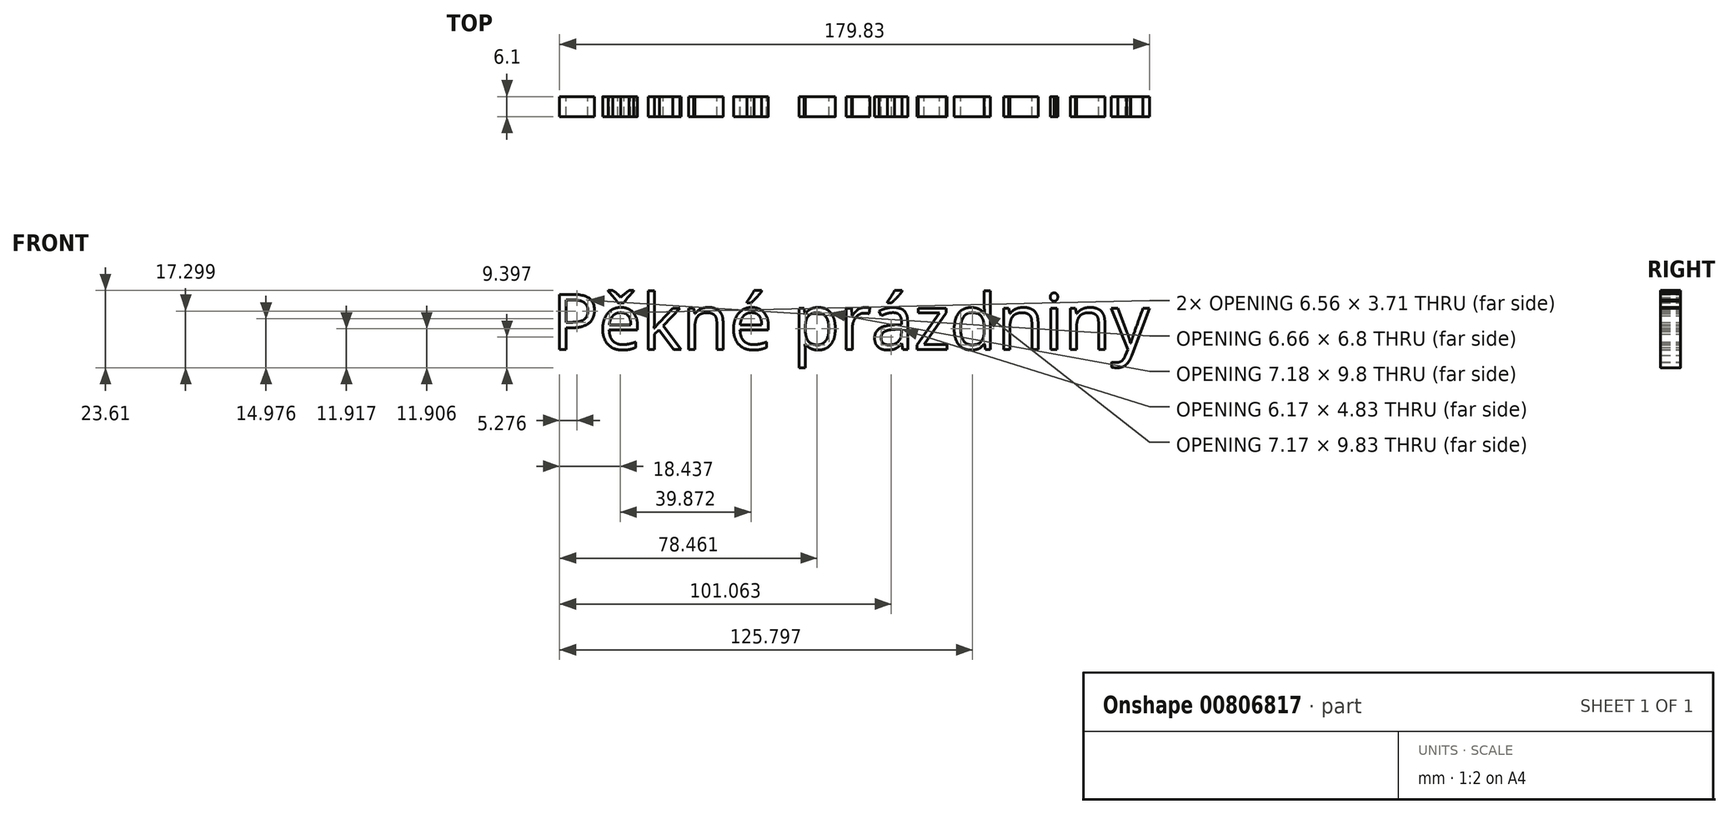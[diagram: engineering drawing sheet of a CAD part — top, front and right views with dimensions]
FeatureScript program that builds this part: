
annotation { "Feature Type Name" : "Feature", "Feature Type Description" : "" }
export const myFeature = defineFeature(function(context is Context, id is Id, definition is map)
    precondition{}
    {
        {
            var Q0;
            Q0=qCreatedBy(makeId("Front.planeOp"),FACE);
            var sketch = newSketch(context, id + "F0", { "sketchPlane" : qUnion([Q0])});
            skText(sketch, "E0", { "text": "Pěkné prázdniny\n", "fontName": "OpenSans-Regular.ttf"});
            const initialGuessF0  = {"E0": [-0.0668, 0, 1, 0, 0.01689]};
            skSetInitialGuess(sketch, initialGuessF0);
            skSolve(sketch);
        }
        {
            var Q0;
            Q0 = qSketchRegion(id + "F0", true);
            extrude(context, id + "F1", {"entities" : qUnion([Q0]), "depth" : 6.1 * mm, "offsetDistance" : 25.4 * mm});
        }
    });
